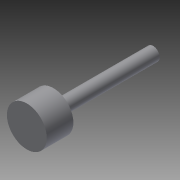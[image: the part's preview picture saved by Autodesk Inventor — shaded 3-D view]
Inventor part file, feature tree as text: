
AUTODESK INVENTOR PART (.ipt)
format: ipt  version: 2015 (Build 190159000, 159)  size: 78,336 bytes
history: native  units: mm
features: extrude x2, sketch x2
ambient origin geometry x8: Origin, YZ Plane, XZ Plane, XY Plane, X Axis, Y Axis, Z Axis, Center Point
bodies: Solid1 (feature_tree)
feature tree (4):
  extrude  "Extrusion1"  Depth=4.0mm TaperAngle=0.0deg
  extrude  "Extrusion2"  Depth=15.0mm TaperAngle=0.0deg
  sketch  "Sketch1"  dims[d0=6.0mm d1=4.0mm d2=0.0mm]
  sketch  "Sketch2"  dims[d3=2.0mm d4=15.0mm d5=0.0mm]
